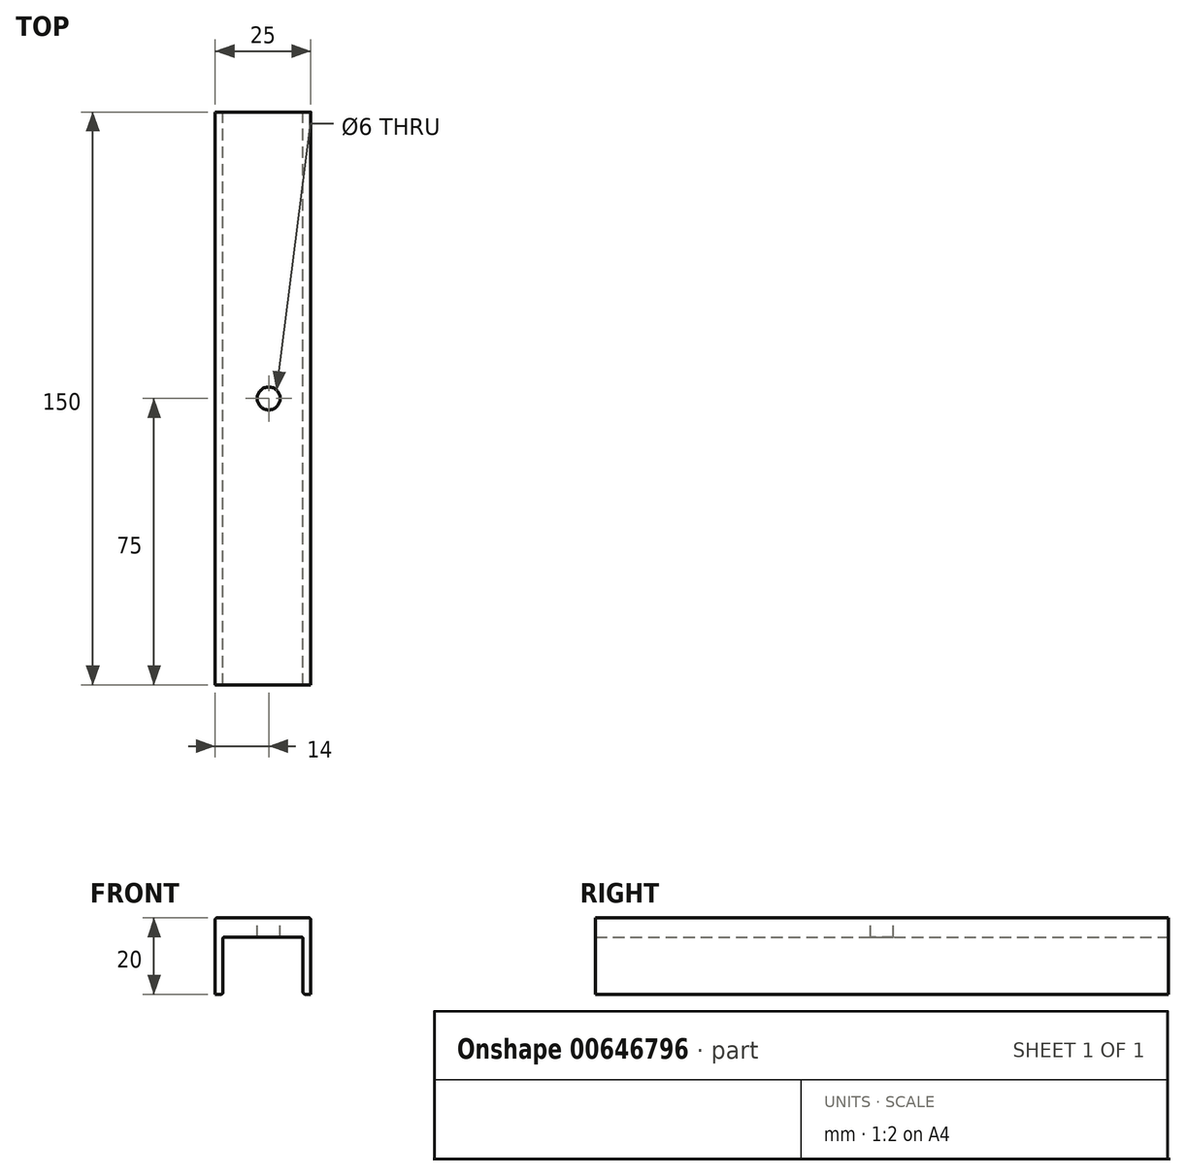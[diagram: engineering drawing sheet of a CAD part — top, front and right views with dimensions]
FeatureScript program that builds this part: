
annotation { "Feature Type Name" : "Feature", "Feature Type Description" : "" }
export const myFeature = defineFeature(function(context is Context, id is Id, definition is map)
    precondition{}
    {
        {
            var Q0;
            Q0=qCreatedBy(makeId("Front.planeOp"),FACE);
            var sketch = newSketch(context, id + "F0", { "sketchPlane" : qUnion([Q0])});
            skLineSegment(sketch, "E0", {"start": v(0, 20) * mm, "end": v(0, 0) * mm});
            skLineSegment(sketch, "E1", {"start": v(0, 0) * mm, "end": v(2, 0) * mm});
            skLineSegment(sketch, "E2", {"start": v(2, 0) * mm, "end": v(2, 15) * mm});
            skLineSegment(sketch, "E3", {"start": v(23, 15) * mm, "end": v(23, 0) * mm});
            skLineSegment(sketch, "E4", {"start": v(23, 0) * mm, "end": v(25, 0) * mm});
            skLineSegment(sketch, "E5", {"start": v(25, 0) * mm, "end": v(25, 20) * mm});
            skLineSegment(sketch, "E6", {"start": v(25, 20) * mm, "end": v(0, 20) * mm});
            skLineSegment(sketch, "E7", {"start": v(2, 15) * mm, "end": v(23, 15) * mm});
            skSolve(sketch);
        }
        {
            var Q0;
            Q0=qSketchRegion(id+"F0",true);
            extrude(context, id + "F1", {"entities" : qUnion([Q0]), "endBound" : BoundingType.SYMMETRIC, "depth" : 150 * mm, "offsetDistance" : 25 * mm});
        }
        {
            var Q0;
            Q0=makeQuery(id+"F1.opExtrude","SWEPT_FACE",FACE,{"disambiguationData":[OSD([sQuery(id+"F0.wireOp",EDGE,"E6")])]});
            var sketch = newSketch(context, id + "F2", { "sketchPlane" : qUnion([Q0])});
            skCircle(sketch, "E8", {"center": v(14, 0) * mm, "radius": 3 * mm});
            skSolve(sketch);
        }
        {
            var Q0;
            Q0=makeQuery(id+"F2.imprint","IMPRINT",FACE,{"disambiguationData":[TD([[makeQuery(id+"F2.imprint","IMPRINT",EDGE,{"derivedFrom":sQuery(id+"F2.wireOp",EDGE,"E8")}),1.0]])]});
            extrude(context, id + "F3", {"entities" : qUnion([Q0]), "operationType" : NewBodyOperationType.REMOVE, "endBound" : BoundingType.UP_TO_NEXT, "oppositeDirection" : true, "depth" : 25 * mm, "offsetDistance" : 25 * mm});
        }
        {
            var Q0;
            Q0=makeQuery(id+"F1.opExtrude","SWEPT_EDGE",EDGE,{"disambiguationData":[OSD([sQuery(id+"F0.wireOp",EDGE,"E0"),sQuery(id+"F0.wireOp",EDGE,"E6")])]});
            var Q1;
            Q1=makeQuery(id+"F1.opExtrude","SWEPT_EDGE",EDGE,{"disambiguationData":[OSD([sQuery(id+"F0.wireOp",EDGE,"E5"),sQuery(id+"F0.wireOp",EDGE,"E6")])]});
            var Q2;
            Q2=makeQuery(id+"F1.opExtrude","SWEPT_EDGE",EDGE,{"disambiguationData":[OSD([sQuery(id+"F0.wireOp",EDGE,"E2"),sQuery(id+"F0.wireOp",EDGE,"5D46qFQe-UmXA-BcV9-RR1S-OxmLbhrvSHBb")])]});
            var Q3;
            Q3=makeQuery(id+"F1.opExtrude","SWEPT_EDGE",EDGE,{"disambiguationData":[OSD([sQuery(id+"F0.wireOp",EDGE,"5D46qFQe-UmXA-BcV9-RR1S-OxmLbhrvSHBb"),sQuery(id+"F0.wireOp",EDGE,"E3")])]});
            fillet(context, id + "F4", {"entities" : qUnion([Q0, Q1, Q2, Q3]), "radius" : .5 * mm, "tangentPropagation" : true, "allowEdgeOverflow" : false});
        }
    });
